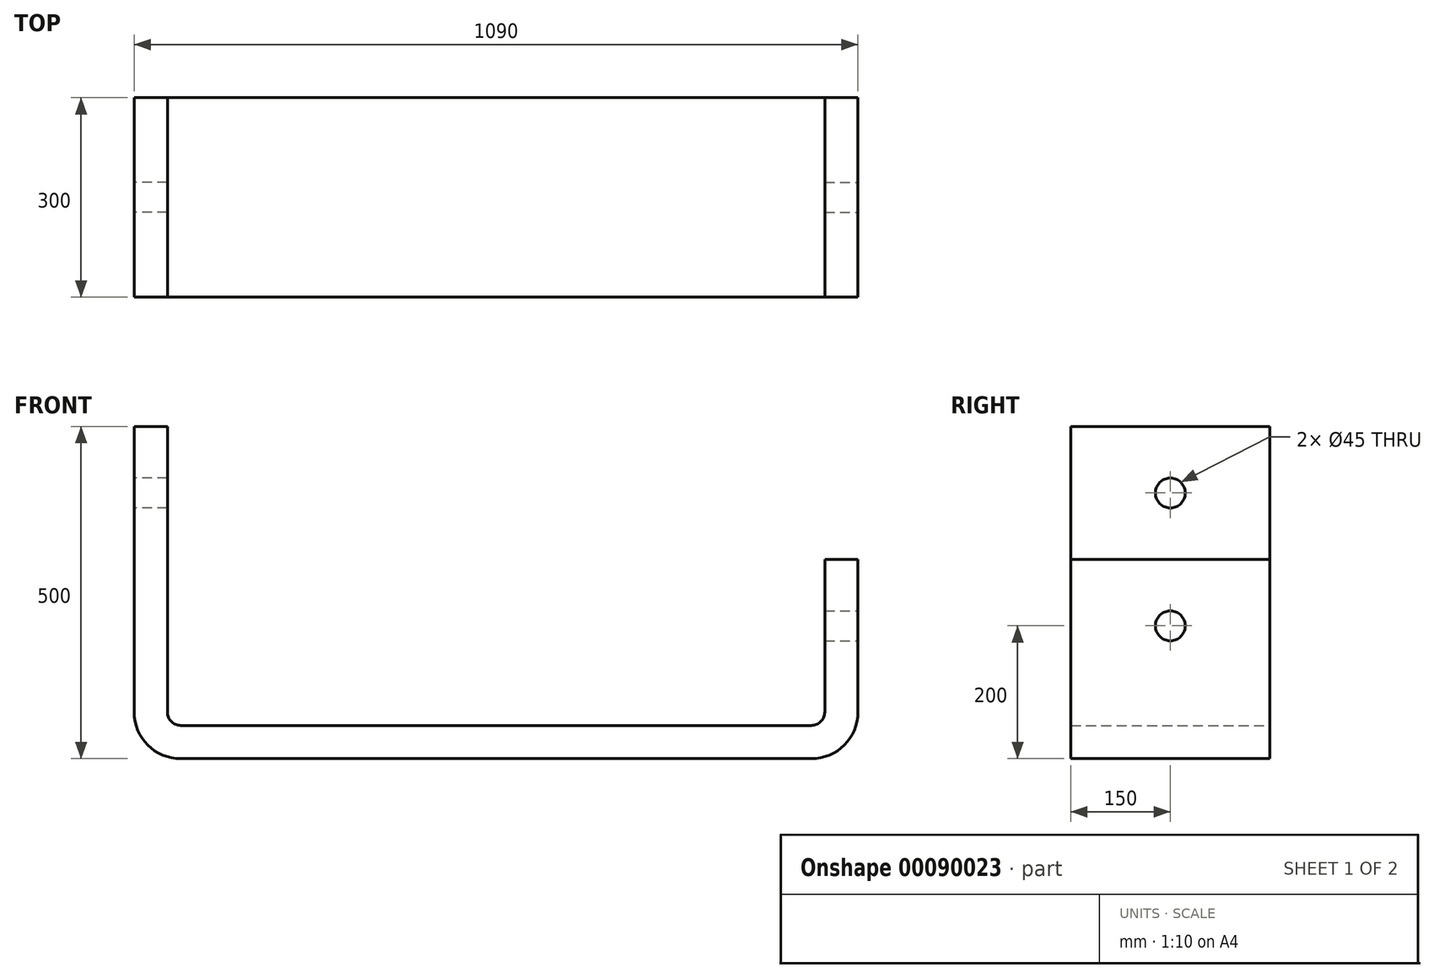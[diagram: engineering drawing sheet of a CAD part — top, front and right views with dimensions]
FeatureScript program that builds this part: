
annotation { "Feature Type Name" : "Feature", "Feature Type Description" : "" }
export const myFeature = defineFeature(function(context is Context, id is Id, definition is map)
    precondition{}
    {
        {
            var Q0;
            Q0=qCreatedBy(makeId("Front.planeOp"),FACE);
            var sketch = newSketch(context, id + "F0", { "sketchPlane" : qUnion([Q0])});
            skLineSegment(sketch, "E0", {"start": v(70, 0) * mm, "end": v(1020, 0) * mm});
            skLineSegment(sketch, "E1", {"start": v(0, 70) * mm, "end": v(0, 500) * mm});
            skLineSegment(sketch, "E2", {"start": v(1090, 70) * mm, "end": v(1090, 300) * mm});
            skLineSegment(sketch, "E3.0", {"start": v(50, 70) * mm, "end": v(50, 500) * mm});
            skLineSegment(sketch, "E4.0", {"start": v(1040, 70) * mm, "end": v(1040, 300) * mm});
            skLineSegment(sketch, "E5.0", {"start": v(70, 50) * mm, "end": v(1020, 50) * mm});
            skLineSegment(sketch, "E6", {"start": v(0, 500) * mm, "end": v(50, 500) * mm});
            skLineSegment(sketch, "E7", {"start": v(1040, 300) * mm, "end": v(1090, 300) * mm});
            skPoint(sketch, "E8.visualSharp", {"position": v(1090, 0) * mm});
            skArc(sketch, "E8.filletArc", {"start": v(1020, 0) * mm, "mid": v(1069.5, 20.5) * mm, "end": v(1090, 70) * mm});
            skPoint(sketch, "E9.visualSharp", {"position": v(0, 0) * mm});
            skArc(sketch, "E9.filletArc", {"start": v(0, 70) * mm, "mid": v(20.5, 20.5) * mm, "end": v(70, 0) * mm});
            skPoint(sketch, "E10.visualSharp", {"position": v(50, 50) * mm});
            skArc(sketch, "E10.filletArc", {"start": v(50, 70) * mm, "mid": v(55.86, 55.86) * mm, "end": v(70, 50) * mm});
            skPoint(sketch, "E11.visualSharp", {"position": v(1040, 50) * mm});
            skArc(sketch, "E11.filletArc", {"start": v(1020, 50) * mm, "mid": v(1034.14, 55.86) * mm, "end": v(1040, 70) * mm});
            skSolve(sketch);
        }
        {
            var Q0;
            Q0=makeQuery(id+"F0.imprint","IMPRINT",FACE,{"disambiguationData":[TD([[makeQuery(id+"F0.imprint","IMPRINT",EDGE,{"derivedFrom":sQuery(id+"F0.wireOp",EDGE,"E0")}),1.0]])]});
            extrude(context, id + "F1", {"entities" : qUnion([Q0]), "depth" : 300 * mm, "symmetric" : true});
        }
        {
            var Q0;
            Q0=makeQuery(id+"F1.opExtrude","SWEPT_FACE",FACE,{"disambiguationData":[OSD([sQuery(id+"F0.wireOp",EDGE,"E2")])]});
            var sketch = newSketch(context, id + "F2", { "sketchPlane" : qUnion([Q0])});
            skCircle(sketch, "E12", {"center": v(0, 200) * mm, "radius": 22.5 * mm});
            skSolve(sketch);
        }
        {
            var Q0;
            Q0=makeQuery(id+"F2.imprint","IMPRINT",FACE,{"disambiguationData":[TD([[makeQuery(id+"F2.imprint","IMPRINT",EDGE,{"derivedFrom":sQuery(id+"F2.wireOp",EDGE,"E12")}),1.0]])]});
            var Q1;
            Q1=makeQuery(id+"F1.opExtrude","SWEPT_FACE",FACE,{"disambiguationData":[OSD([sQuery(id+"F0.wireOp",EDGE,"E4.0")])]});
            extrude(context, id + "F3", {"entities" : qUnion([Q0]), "operationType" : NewBodyOperationType.REMOVE, "endBound" : BoundingType.UP_TO_SURFACE, "oppositeDirection" : true, "endBoundEntityFace" : qUnion([Q1]), "depth" : 25 * mm});
        }
        {
            var Q0;
            Q0=makeQuery(id+"F1.opExtrude","SWEPT_FACE",FACE,{"disambiguationData":[OSD([sQuery(id+"F0.wireOp",EDGE,"E1")])]});
            var sketch = newSketch(context, id + "F4", { "sketchPlane" : qUnion([Q0])});
            skCircle(sketch, "E13", {"center": v(0, 400) * mm, "radius": 22.5 * mm});
            skSolve(sketch);
        }
        {
            var Q0;
            Q0=makeQuery(id+"F4.imprint","IMPRINT",FACE,{"disambiguationData":[TD([[makeQuery(id+"F4.imprint","IMPRINT",EDGE,{"derivedFrom":sQuery(id+"F4.wireOp",EDGE,"E13")}),1.0]])]});
            extrude(context, id + "F5", {"entities" : qUnion([Q0]), "operationType" : NewBodyOperationType.REMOVE, "endBound" : BoundingType.UP_TO_NEXT, "oppositeDirection" : true, "depth" : 25 * mm});
        }
    });
